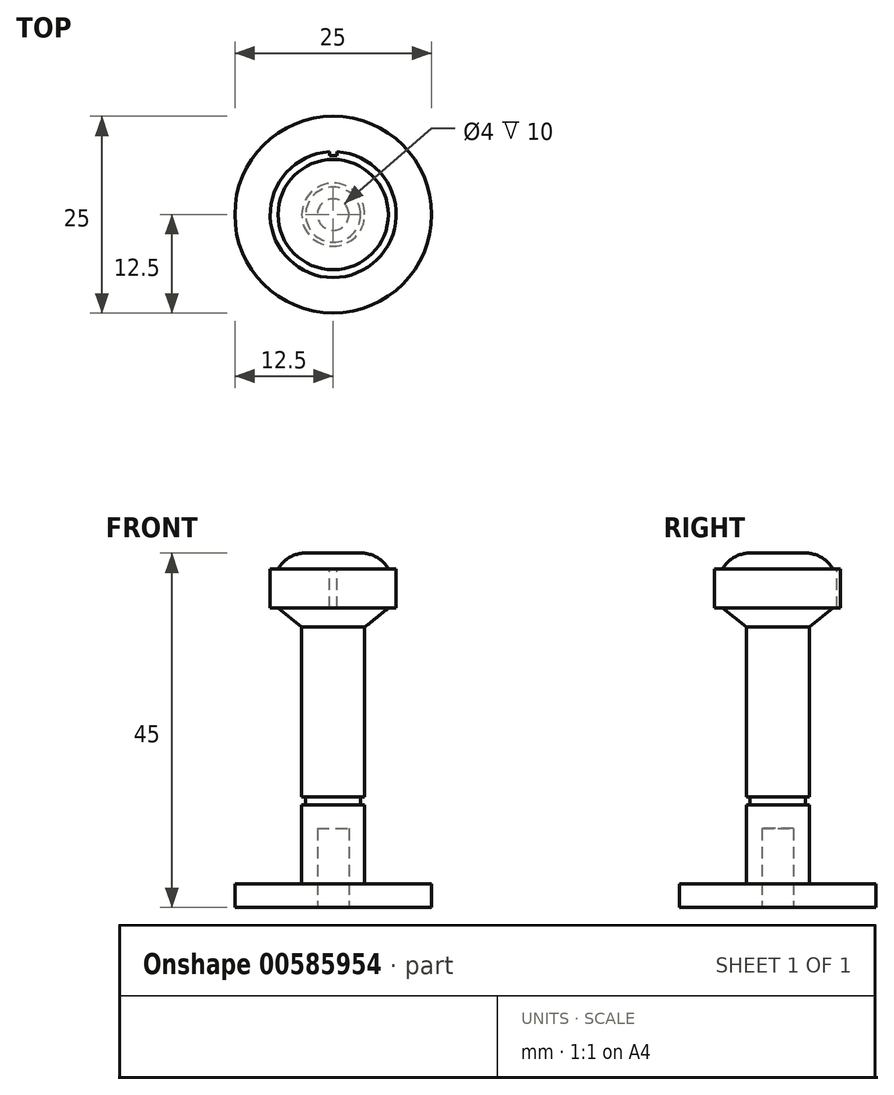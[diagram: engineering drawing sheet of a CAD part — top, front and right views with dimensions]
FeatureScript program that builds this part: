
annotation { "Feature Type Name" : "Feature", "Feature Type Description" : "" }
export const myFeature = defineFeature(function(context is Context, id is Id, definition is map)
    precondition{}
    {
        {
            var Q0;
            Q0=qCreatedBy(makeId("Top.planeOp"),FACE);
            var sketch = newSketch(context, id + "F0", { "sketchPlane" : qUnion([Q0])});
            skCircle(sketch, "E0", {"center": v(0, 0) * mm, "radius": 12.5 * mm});
            skSolve(sketch);
        }
        {
            var Q0;
            Q0 = qSketchRegion(id + "F0", true);
            extrude(context, id + "F1", {"entities" : qUnion([Q0]), "depth" : 3 * mm, "offsetDistance" : 25 * mm});
        }
        {
            var Q0;
            Q0=makeQuery(id+"F1.opExtrude","CAP_FACE",FACE,{"disambiguationData":[OSD([sQuery(id+"F0.wireOp",EDGE,"E0")])],"isStart":false});
            var sketch = newSketch(context, id + "F2", { "sketchPlane" : qUnion([Q0])});
            skCircle(sketch, "E1", {"center": v(0, 0) * mm, "radius": 4 * mm});
            skSolve(sketch);
        }
        {
            var Q0;
            Q0 = qSketchRegion(id + "F2", true);
            extrude(context, id + "F3", {"entities" : qUnion([Q0]), "operationType" : NewBodyOperationType.ADD, "depth" : 10 * mm, "offsetDistance" : 25 * mm});
        }
        {
            var Q0;
            Q0=makeQuery(id+"F3.opExtrude","CAP_FACE",FACE,{"disambiguationData":[OSD([sQuery(id+"F2.wireOp",EDGE,"E1")])],"isStart":false});
            var sketch = newSketch(context, id + "F4", { "sketchPlane" : qUnion([Q0])});
            skCircle(sketch, "E2", {"center": v(0, 0) * mm, "radius": 3.5 * mm});
            skSolve(sketch);
        }
        {
            var Q0;
            Q0 = qSketchRegion(id + "F4", true);
            extrude(context, id + "F5", {"entities" : qUnion([Q0]), "operationType" : NewBodyOperationType.ADD, "depth" : 1 * mm, "offsetDistance" : 25 * mm});
        }
        {
            var Q0;
            Q0=makeQuery(id+"F5.opExtrude","CAP_FACE",FACE,{"disambiguationData":[OSD([sQuery(id+"F4.wireOp",EDGE,"E2")])],"isStart":false});
            var sketch = newSketch(context, id + "F6", { "sketchPlane" : qUnion([Q0])});
            skCircle(sketch, "E3", {"center": v(0, 0) * mm, "radius": 4 * mm});
            skSolve(sketch);
        }
        {
            var Q0;
            Q0 = qSketchRegion(id + "F6", true);
            extrude(context, id + "F7", {"entities" : qUnion([Q0]), "operationType" : NewBodyOperationType.ADD, "depth" : 20 * mm, "offsetDistance" : 25 * mm});
        }
        {
            var Q0;
            Q0=makeQuery(id+"F7.opExtrude","CAP_FACE",FACE,{"disambiguationData":[OSD([sQuery(id+"F6.wireOp",EDGE,"E3")])],"isStart":false});
            var sketch = newSketch(context, id + "F8", { "sketchPlane" : qUnion([Q0])});
            skCircle(sketch, "E4", {"center": v(0, 0) * mm, "radius": 7 * mm});
            skSolve(sketch);
        }
        {
            var Q0;
            Q0 = qSketchRegion(id + "F8", true);
            extrude(context, id + "F9", {"entities" : qUnion([Q0]), "operationType" : NewBodyOperationType.ADD, "depth" : 4 * mm, "offsetDistance" : 25 * mm});
        }
        {
            var Q0;
            Q0=makeQuery(id+"F9.opExtrude","CAP_FACE",FACE,{"disambiguationData":[OSD([sQuery(id+"F8.wireOp",EDGE,"E4")])],"isStart":false});
            var sketch = newSketch(context, id + "F10", { "sketchPlane" : qUnion([Q0])});
            skCircle(sketch, "E5", {"center": v(0, 0) * mm, "radius": 8 * mm});
            skSolve(sketch);
        }
        {
            var Q0;
            Q0 = qSketchRegion(id + "F10", true);
            extrude(context, id + "F11", {"entities" : qUnion([Q0]), "operationType" : NewBodyOperationType.ADD, "depth" : 5 * mm, "offsetDistance" : 25 * mm});
        }
        {
            var Q0;
            Q0=makeQuery(id+"F11.opExtrude","CAP_FACE",FACE,{"disambiguationData":[OSD([sQuery(id+"F10.wireOp",EDGE,"E5")])],"isStart":false});
            var sketch = newSketch(context, id + "F12", { "sketchPlane" : qUnion([Q0])});
            skCircle(sketch, "E6", {"center": v(0, 0) * mm, "radius": 7 * mm});
            skSolve(sketch);
        }
        {
            var Q0;
            Q0 = qSketchRegion(id + "F12", true);
            extrude(context, id + "F13", {"entities" : qUnion([Q0]), "operationType" : NewBodyOperationType.ADD, "depth" : 2 * mm, "offsetDistance" : 25 * mm});
        }
        {
            var Q0;
            Q0=makeQuery(id+"F9.opExtrude","CAP_EDGE",EDGE,{"disambiguationData":[OSD([sQuery(id+"F8.wireOp",EDGE,"E4")])],"isStart":true});
            chamfer(context, id + "F14", {"entities" : qUnion([Q0]), "chamferType" : ChamferType.TWO_OFFSETS, "width1" : 4 * mm, "oppositeDirection" : false, "width2" : 5 * mm, "tangentPropagation" : true});
        }
        {
            var Q0;
            Q0=makeQuery(id+"F13.opExtrude","CAP_EDGE",EDGE,{"disambiguationData":[OSD([sQuery(id+"F12.wireOp",EDGE,"E6")])],"isStart":false});
            fillet(context, id + "F15", {"entities" : qUnion([Q0]), "radius" : 4 * mm, "tangentPropagation" : true, "allowEdgeOverflow" : false});
        }
        {
            var Q0;
            Q0=makeQuery(id+"F1.opExtrude","CAP_FACE",FACE,{"disambiguationData":[OSD([sQuery(id+"F0.wireOp",EDGE,"E0")])],"isStart":true});
            var sketch = newSketch(context, id + "F16", { "sketchPlane" : qUnion([Q0])});
            skCircle(sketch, "E7", {"center": v(0, 0) * mm, "radius": 2 * mm});
            skSolve(sketch);
        }
        {
            var Q0;
            Q0=makeQuery(id+"F16.imprint","IMPRINT",FACE,{"disambiguationData":[TD([[makeQuery(id+"F16.imprint","IMPRINT",EDGE,{"derivedFrom":sQuery(id+"F16.wireOp",EDGE,"E7")}),1.0]])]});
            extrude(context, id + "F17", {"entities" : qUnion([Q0]), "operationType" : NewBodyOperationType.REMOVE, "oppositeDirection" : true, "depth" : 10 * mm, "offsetDistance" : 25 * mm});
        }
        {
            var Q0;
            Q0=makeQuery(id+"F11.opExtrude","CAP_FACE",FACE,{"disambiguationData":[OSD([sQuery(id+"F10.wireOp",EDGE,"E5")])],"isStart":false});
            var sketch = newSketch(context, id + "F18", { "sketchPlane" : qUnion([Q0])});
            skLineSegment(sketch, "E8.bottom", {"start": v(-0.5, 8.5) * mm, "end": v(0.5, 8.5) * mm});
            skLineSegment(sketch, "E8.top", {"start": v(-0.5, 7.5) * mm, "end": v(0.5, 7.5) * mm});
            skLineSegment(sketch, "E8.left", {"start": v(-0.5, 8.5) * mm, "end": v(-0.5, 7.5) * mm});
            skLineSegment(sketch, "E8.right", {"start": v(0.5, 8.5) * mm, "end": v(0.5, 7.5) * mm});
            skPoint(sketch, "E8.middle", {"position": v(0, 8) * mm});
            skSolve(sketch);
        }
        {
            var Q0;
            {var subQ0=sQuery(id+"F18.wireOp",EDGE,"E8.top");Q0=makeQuery(id+"F18.imprint","IMPRINT",FACE,{"disambiguationData":[TD([[makeQuery(id+"F18.imprint","IMPRINT",EDGE,{"derivedFrom":subQ0}),1.0]])]});}
            extrude(context, id + "F19", {"entities" : qUnion([Q0]), "operationType" : NewBodyOperationType.REMOVE, "oppositeDirection" : true, "depth" : 25 * mm, "offsetDistance" : 25 * mm});
        }
    });
